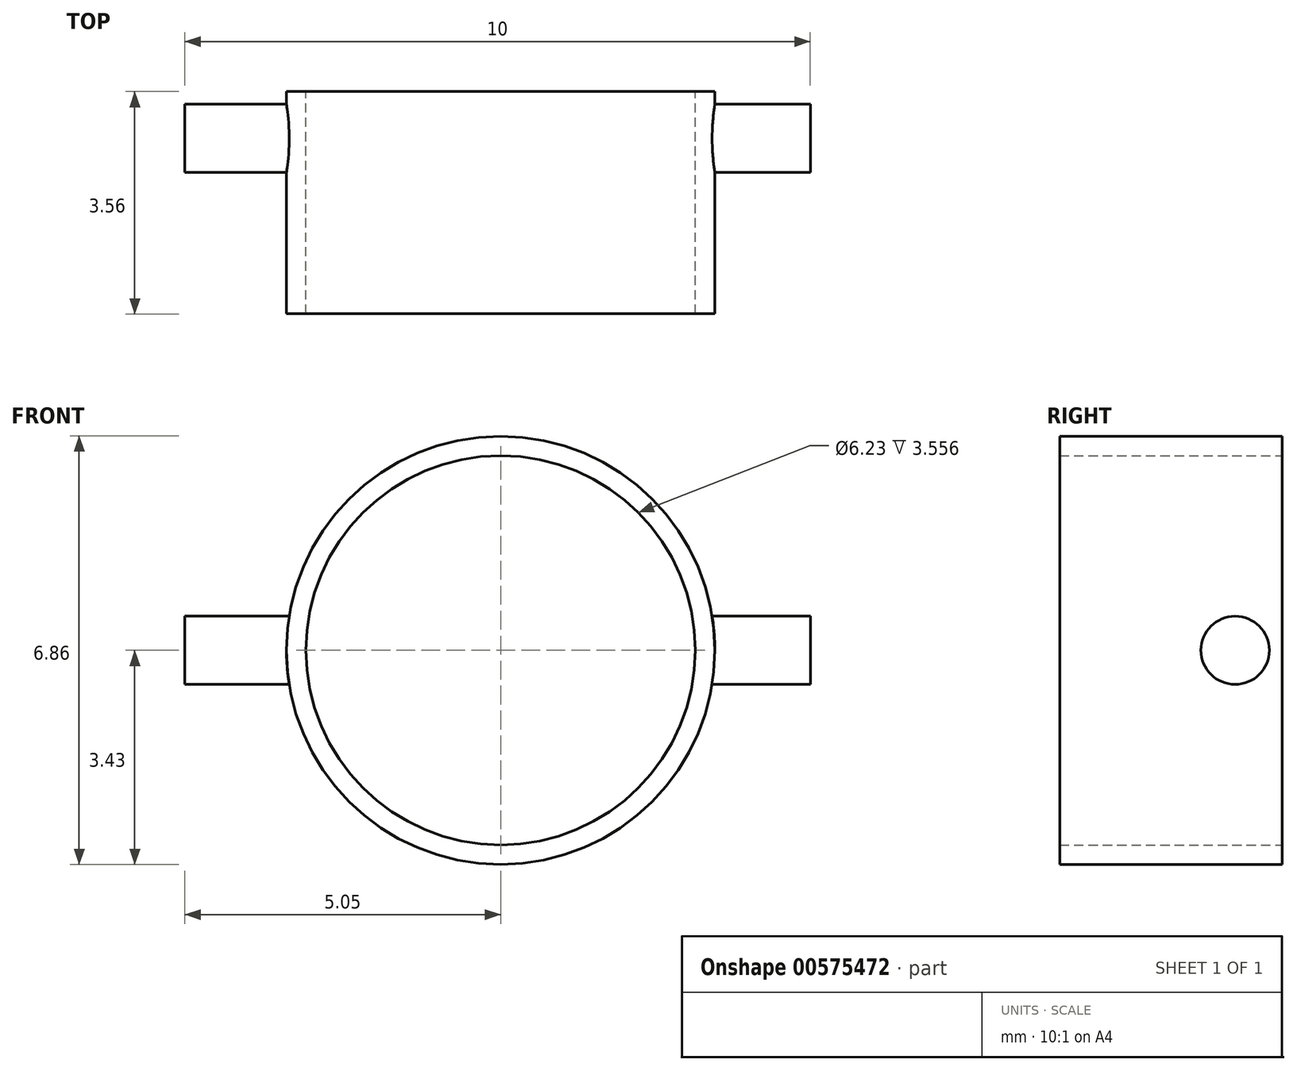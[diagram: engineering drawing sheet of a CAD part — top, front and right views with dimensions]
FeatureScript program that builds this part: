
annotation { "Feature Type Name" : "Feature", "Feature Type Description" : "" }
export const myFeature = defineFeature(function(context is Context, id is Id, definition is map)
    precondition{}
    {
        {
            var Q0;
            Q0=qCreatedBy(makeId("Front.planeOp"),FACE);
            var sketch = newSketch(context, id + "F0", { "sketchPlane" : qUnion([Q0])});
            skCircle(sketch, "E0", {"center": v(0, 0) * mm, "radius": 3.11 * mm});
            skCircle(sketch, "E1", {"center": v(0, 0) * mm, "radius": 3.43 * mm});
            skSolve(sketch);
        }
        {
            var Q0;
            Q0=makeQuery(id+"F0.imprint","IMPRINT",FACE,{"disambiguationData":[TD([[makeQuery(id+"F0.imprint","IMPRINT",EDGE,{"derivedFrom":sQuery(id+"F0.wireOp",EDGE,"E0")}),-1.0]])]});
            extrude(context, id + "F1", {"entities" : qUnion([Q0]), "depth" : 3.56 * mm, "offsetDistance" : 25.4 * mm});
        }
        {
            var Q0;
            Q0=qCreatedBy(makeId("Right.planeOp"),FACE);
            var sketch = newSketch(context, id + "F2", { "sketchPlane" : qUnion([Q0])});
            skCircle(sketch, "E2", {"center": v(-0.75, 0) * mm, "radius": 0.55 * mm});
            skSolve(sketch);
        }
        {
            var Q0;
            Q0=makeQuery(id+"F2.imprint","IMPRINT",FACE,{"disambiguationData":[TD([[makeQuery(id+"F2.imprint","IMPRINT",EDGE,{"derivedFrom":sQuery(id+"F2.wireOp",EDGE,"E2")}),1.0]])]});
            extrude(context, id + "F3", {"entities" : qUnion([Q0]), "operationType" : NewBodyOperationType.ADD, "depth" : 4.95 * mm, "offsetDistance" : 25.4 * mm, "hasSecondDirection" : true, "secondDirectionOppositeDirection" : false, "secondDirectionDepth" : 3.2 * mm});
        }
        {
            var Q0;
            Q0=makeQuery(id+"F2.imprint","IMPRINT",FACE,{"disambiguationData":[TD([[makeQuery(id+"F2.imprint","IMPRINT",EDGE,{"derivedFrom":sQuery(id+"F2.wireOp",EDGE,"E2")}),1.0]])]});
            extrude(context, id + "F4", {"entities" : qUnion([Q0]), "operationType" : NewBodyOperationType.ADD, "oppositeDirection" : true, "depth" : 5.05 * mm, "offsetDistance" : 25.4 * mm, "hasSecondDirection" : true, "secondDirectionOppositeDirection" : true, "secondDirectionDepth" : 3.17 * mm});
        }
    });
